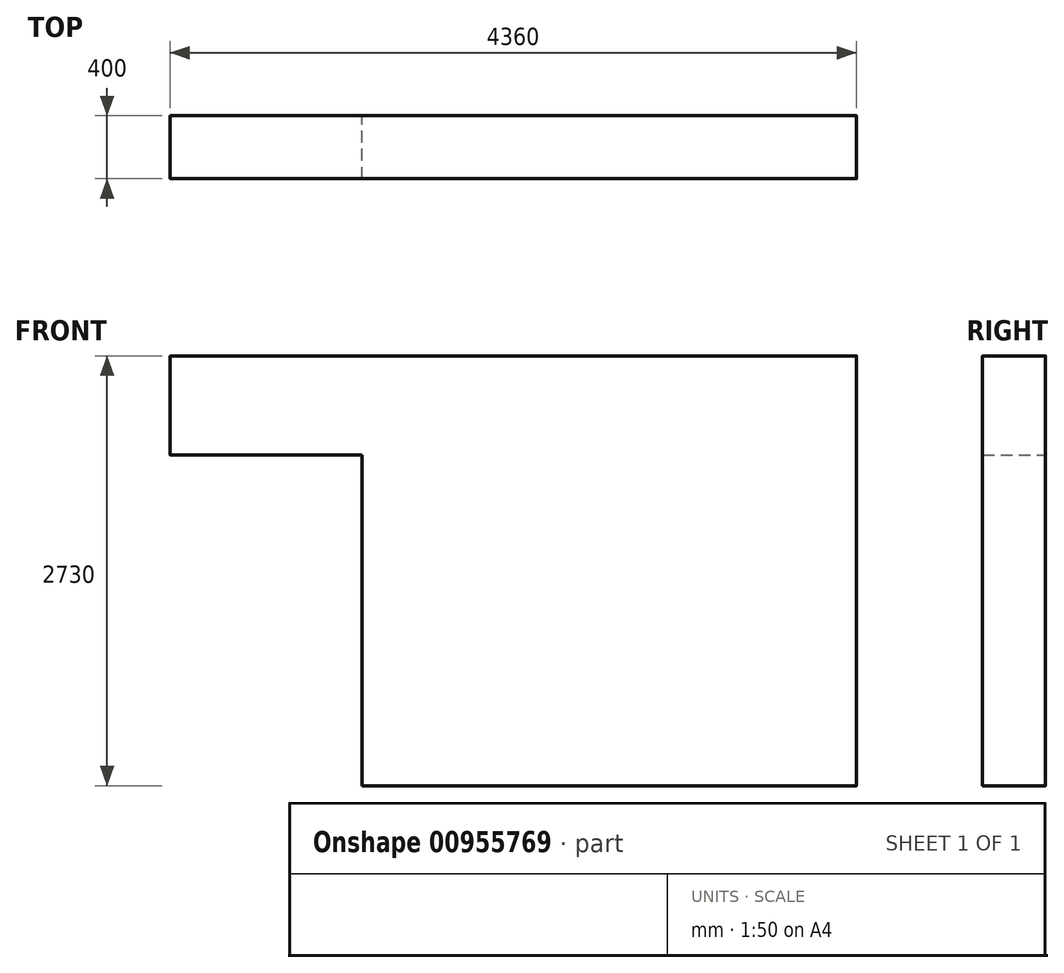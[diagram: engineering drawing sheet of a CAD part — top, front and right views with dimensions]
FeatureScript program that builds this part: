
annotation { "Feature Type Name" : "Feature", "Feature Type Description" : "" }
export const myFeature = defineFeature(function(context is Context, id is Id, definition is map)
    precondition{}
    {
        {
            var Q0;
            Q0=qCreatedBy(makeId("Front.planeOp"),FACE);
            var sketch = newSketch(context, id + "F0", { "sketchPlane" : qUnion([Q0])});
            skLineSegment(sketch, "E0.bottom", {"start": v(-2509.75, 2730) * mm, "end": v(1850.25, 2730) * mm});
            skLineSegment(sketch, "E0.top", {"start": v(-2509.75, 0) * mm, "end": v(1850.25, 0) * mm});
            skLineSegment(sketch, "E0.left", {"start": v(-2509.75, 2730) * mm, "end": v(-2509.75, 0) * mm});
            skLineSegment(sketch, "E0.right", {"start": v(1850.25, 2730) * mm, "end": v(1850.25, 0) * mm});
            skLineSegment(sketch, "E1", {"start": v(-2509.75, 0) * mm, "end": v(-1289.75, 0) * mm});
            skLineSegment(sketch, "E2", {"start": v(-1289.75, 0) * mm, "end": v(-1289.75, 2100) * mm});
            skLineSegment(sketch, "E3", {"start": v(-1289.75, 2100) * mm, "end": v(-2509.75, 2100) * mm});
            skSolve(sketch);
        }
        {
            var Q0;
            {var subQ1=sQuery(id+"F0.wireOp",EDGE,"E0.bottom");Q0=makeQuery(id+"F0.imprint","IMPRINT",FACE,{"disambiguationData":[TD([[makeQuery(id+"F0.imprint","IMPRINT",EDGE,{"derivedFrom":subQ1}),-1.0]])]});}
            extrude(context, id + "F1", {"entities" : qUnion([Q0]), "depth" : 400 * mm, "offsetDistance" : 25.4 * mm});
        }
        {
            var Q0;
            Q0=makeQuery(id+"F1.opExtrude","CAP_EDGE",EDGE,{"disambiguationData":[OSD([sQuery(id+"F0.wireOp",EDGE,"E0.top")])],"isStart":false});
            fillet(context, id + "F2", {"entities" : qUnion([Q0]), "radius" : ((0.5 * sqrt(2)) / 2) * mm, "tangentPropagation" : true, "allowEdgeOverflow" : false});
        }
        {
            var Q0;
            Q0=makeQuery(id+"F1.opExtrude","CAP_EDGE",EDGE,{"disambiguationData":[OSD([sQuery(id+"F0.wireOp",EDGE,"E0.top")])],"isStart":true});
            fillet(context, id + "F3", {"entities" : qUnion([Q0]), "radius" : ((0.5 * sqrt(2)) / 2) * mm, "tangentPropagation" : true, "allowEdgeOverflow" : false});
        }
        {
            var Q0;
            Q0=makeQuery(id+"F1.opExtrude","CAP_EDGE",EDGE,{"disambiguationData":[OSD([sQuery(id+"F0.wireOp",EDGE,"E0.bottom")])],"isStart":true});
            fillet(context, id + "F4", {"entities" : qUnion([Q0]), "radius" : ((.5 * sqrt(2)) / 2) * mm, "tangentPropagation" : true, "allowEdgeOverflow" : false});
        }
        {
            var Q0;
            Q0=makeQuery(id+"F1.opExtrude","CAP_EDGE",EDGE,{"disambiguationData":[OSD([sQuery(id+"F0.wireOp",EDGE,"E0.bottom")])],"isStart":false});
            fillet(context, id + "F5", {"entities" : qUnion([Q0]), "radius" : ((.5 * sqrt(2)) / 2) * mm, "tangentPropagation" : true, "allowEdgeOverflow" : false});
        }
        {
            var Q0;
            Q0=makeQuery(id+"F1.opExtrude","CAP_EDGE",EDGE,{"disambiguationData":[OSD([sQuery(id+"F0.wireOp",EDGE,"E2")])],"isStart":false});
            fillet(context, id + "F6", {"entities" : qUnion([Q0]), "radius" : ((.5 * sqrt(2)) / 2) * mm, "tangentPropagation" : true, "allowEdgeOverflow" : false});
        }
        {
            var Q0;
            Q0=makeQuery(id+"F1.opExtrude","CAP_EDGE",EDGE,{"disambiguationData":[OSD([sQuery(id+"F0.wireOp",EDGE,"E0.left")])],"isStart":false});
            fillet(context, id + "F7", {"entities" : qUnion([Q0]), "radius" : ((.5 * sqrt(2)) / 2) * mm, "tangentPropagation" : true, "allowEdgeOverflow" : false});
        }
        {
            var Q0;
            Q0=makeQuery(id+"F1.opExtrude","CAP_EDGE",EDGE,{"disambiguationData":[OSD([sQuery(id+"F0.wireOp",EDGE,"E3")])],"isStart":false});
            fillet(context, id + "F8", {"entities" : qUnion([Q0]), "radius" : ((.5 * sqrt(2)) / 2) * mm, "tangentPropagation" : true, "allowEdgeOverflow" : false});
        }
    });
